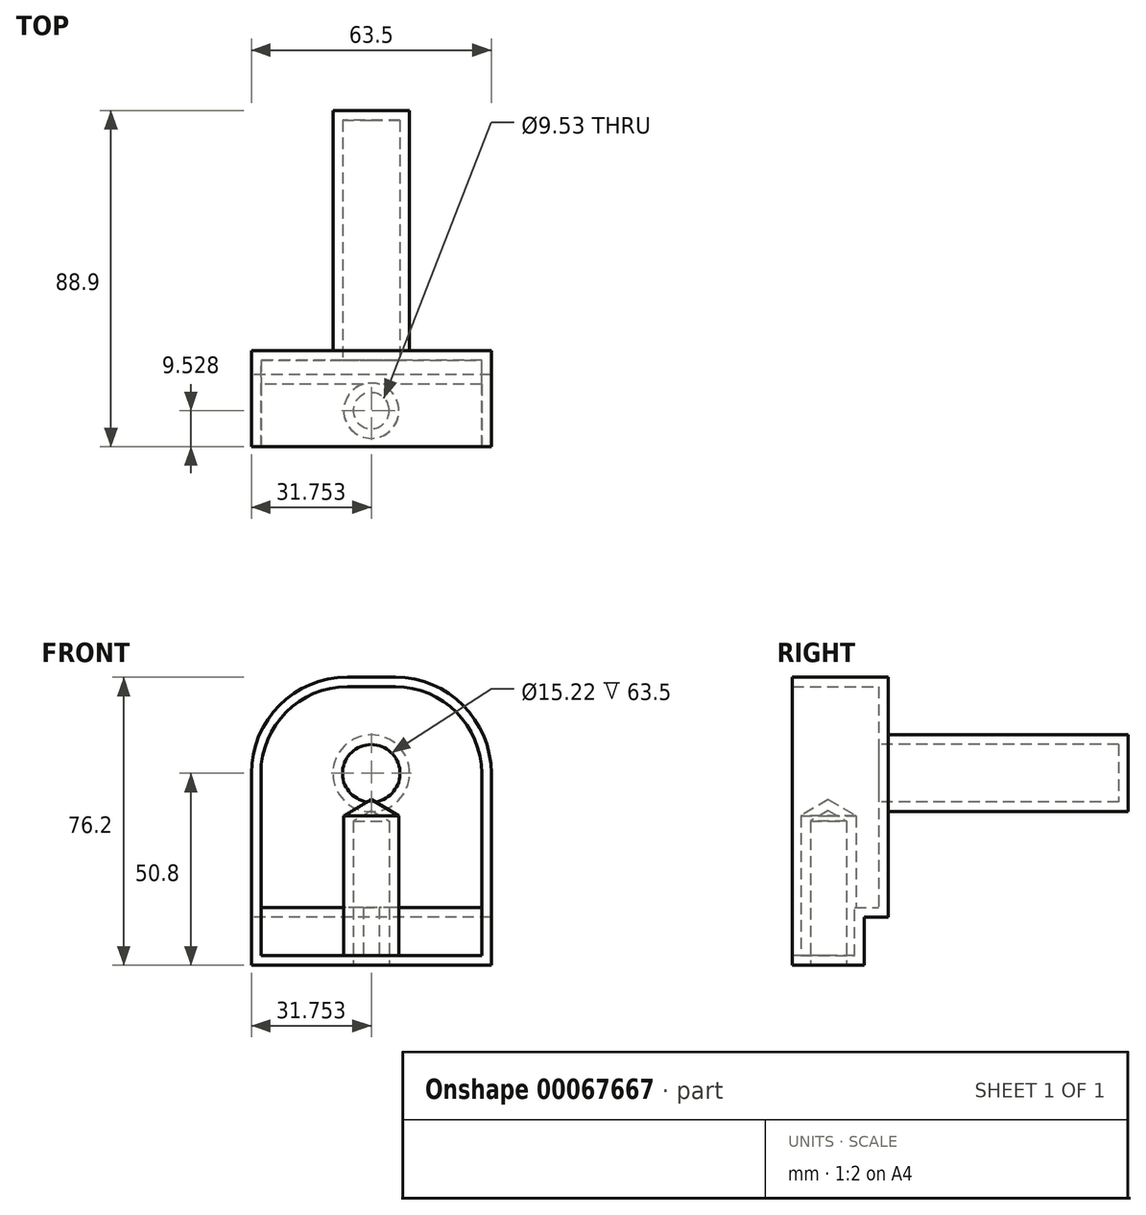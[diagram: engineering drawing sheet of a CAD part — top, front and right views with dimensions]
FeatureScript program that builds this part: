
annotation { "Feature Type Name" : "Feature", "Feature Type Description" : "" }
export const myFeature = defineFeature(function(context is Context, id is Id, definition is map)
    precondition{}
    {
        {
            var Q0;
            Q0=qCreatedBy(makeId("Top.planeOp"),FACE);
            var sketch = newSketch(context, id + "F0", { "sketchPlane" : qUnion([Q0])});
            skLineSegment(sketch, "E0.bottom", {"start": v(-60.63, 0.1) * mm, "end": v(2.87, 0.1) * mm});
            skLineSegment(sketch, "E0.top", {"start": v(-60.63, -25.3) * mm, "end": v(2.87, -25.3) * mm});
            skLineSegment(sketch, "E0.left", {"start": v(-60.63, 0.1) * mm, "end": v(-60.63, -25.3) * mm});
            skLineSegment(sketch, "E0.right", {"start": v(2.87, 0.1) * mm, "end": v(2.87, -25.3) * mm});
            skSolve(sketch);
        }
        {
            var Q0;
            Q0=qSketchRegion(id+"F0",true);
            extrude(context, id + "F1", {"entities" : qUnion([Q0]), "depth" : 76.2 * mm});
        }
        {
            var Q0;
            Q0=makeQuery(id+"F1.opExtrude","SWEPT_FACE",FACE,{"disambiguationData":[OSD([sQuery(id+"F0.wireOp",EDGE,"E0.bottom")])]});
            var sketch = newSketch(context, id + "F2", { "sketchPlane" : qUnion([Q0])});
            skPoint(sketch, "E1", {"position": v(28.88, 50.8) * mm});
            skCircle(sketch, "E2", {"center": v(28.88, 50.8) * mm, "radius": 10.15 * mm});
            skSolve(sketch);
        }
        {
            var Q0;
            Q0=qSketchRegion(id+"F2",true);
            extrude(context, id + "F3", {"entities" : qUnion([Q0]), "operationType" : NewBodyOperationType.ADD, "depth" : 63.5 * mm});
        }
        {
            var Q0;
            Q0=makeQuery(id+"F1.opExtrude","CAP_EDGE",EDGE,{"disambiguationData":[OSD([sQuery(id+"F0.wireOp",EDGE,"E0.right")])],"isStart":false});
            var Q1;
            Q1=makeQuery(id+"F1.opExtrude","CAP_EDGE",EDGE,{"disambiguationData":[OSD([sQuery(id+"F0.wireOp",EDGE,"E0.left")])],"isStart":false});
            fillet(context, id + "F4", {"entities" : qUnion([Q0, Q1]), "radius" : 25.4 * mm, "tangentPropagation" : true, "allowEdgeOverflow" : false});
        }
        {
            var Q0;
            Q0=makeQuery(id+"F1.opExtrude","SWEPT_FACE",FACE,{"disambiguationData":[OSD([sQuery(id+"F0.wireOp",EDGE,"E0.left")])]});
            var sketch = newSketch(context, id + "F5", { "sketchPlane" : qUnion([Q0])});
            skLineSegment(sketch, "E3.bottom", {"start": v(-0.1, 12.7) * mm, "end": v(6.25, 12.7) * mm});
            skLineSegment(sketch, "E3.top", {"start": v(-0.1, 0) * mm, "end": v(6.25, 0) * mm});
            skLineSegment(sketch, "E3.left", {"start": v(-0.1, 12.7) * mm, "end": v(-0.1, 0) * mm});
            skLineSegment(sketch, "E3.right", {"start": v(6.25, 12.7) * mm, "end": v(6.25, 0) * mm});
            skSolve(sketch);
        }
        {
            var Q0;
            Q0=qSketchRegion(id+"F5",true);
            extrude(context, id + "F6", {"entities" : qUnion([Q0]), "operationType" : NewBodyOperationType.REMOVE, "endBound" : BoundingType.THROUGH_ALL, "oppositeDirection" : true, "depth" : 25.4 * mm});
        }
        {
            var Q0;
            Q0=makeQuery(id+"F1.opExtrude","CAP_FACE",FACE,{"disambiguationData":[OSD([sQuery(id+"F0.wireOp",EDGE,"E0.bottom"),sQuery(id+"F0.wireOp",EDGE,"E0.top"),sQuery(id+"F0.wireOp",EDGE,"E0.left"),sQuery(id+"F0.wireOp",EDGE,"E0.right")])],"isStart":true});
            var sketch = newSketch(context, id + "F7", { "sketchPlane" : qUnion([Q0])});
            skPoint(sketch, "E4", {"position": v(-28.88, 15.77) * mm});
            skSolve(sketch);
        }
        {
            var Q0;
            Q0=sQuery(id+"F7.wireOp",VERTEX,"E4");
            var Q1;
            Q1=makeQuery(id+"F1.opExtrude","SWEPT_BODY",BODY,{"disambiguationData":[OSD([sQuery(id+"F0.wireOp",EDGE,"E0.bottom"),sQuery(id+"F0.wireOp",EDGE,"E0.top"),sQuery(id+"F0.wireOp",EDGE,"E0.left"),sQuery(id+"F0.wireOp",EDGE,"E0.right")])]});
            hole(context, id + "F8", {"style" : HoleStyle.SIMPLE, "holeDiameter" : 9.52 * mm, "endStyle" : HoleEndStyle.BLIND, "holeDepth" : 38.1 * mm, "locations" : qUnion([Q0]), "scope" : qUnion([Q1])});
        }
        {
            var Q0;
            Q0=makeQuery(id+"F1.opExtrude","SWEPT_FACE",FACE,{"disambiguationData":[OSD([sQuery(id+"F0.wireOp",EDGE,"E0.top")])]});
            shell(context, id + "F9", {"entities" : qUnion([Q0]), "thickness" : 2.54 * mm});
        }
    });
